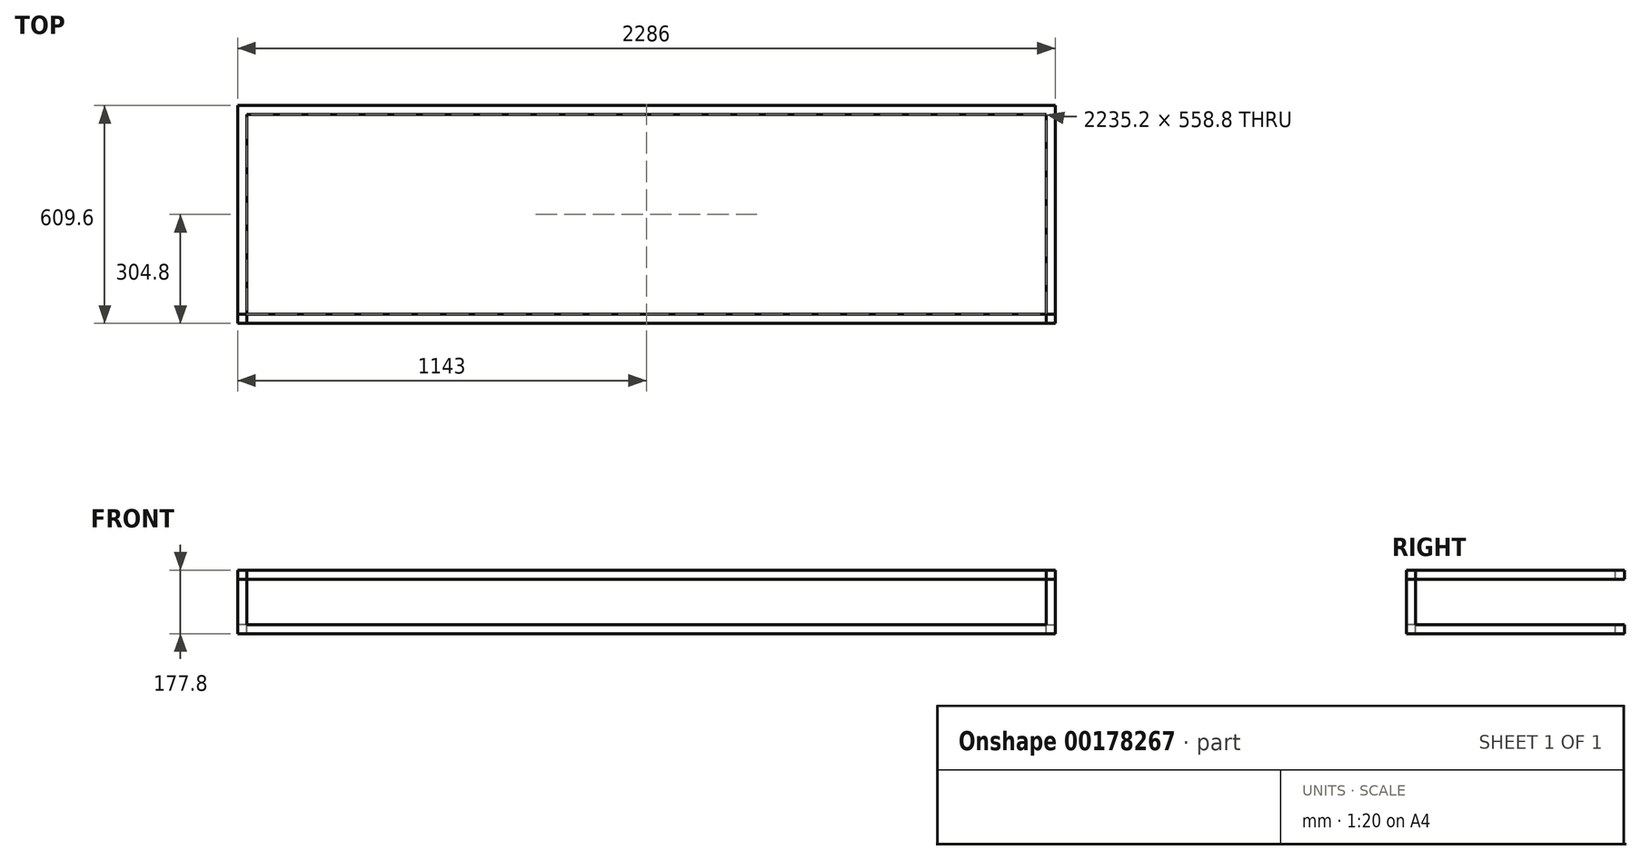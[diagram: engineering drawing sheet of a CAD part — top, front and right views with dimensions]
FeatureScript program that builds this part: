
annotation { "Feature Type Name" : "Feature", "Feature Type Description" : "" }
export const myFeature = defineFeature(function(context is Context, id is Id, definition is map)
    precondition{}
    {
        {
            var Q0;
            Q0=qCreatedBy(makeId("Top.planeOp"),FACE);
            var sketch = newSketch(context, id + "F0", { "sketchPlane" : qUnion([Q0])});
            skLineSegment(sketch, "E0.bottom", {"start": v(-1143, -304.8) * mm, "end": v(1143, -304.8) * mm});
            skLineSegment(sketch, "E0.top", {"start": v(-1143, 304.8) * mm, "end": v(1143, 304.8) * mm});
            skLineSegment(sketch, "E0.left", {"start": v(-1143, -304.8) * mm, "end": v(-1143, 304.8) * mm});
            skLineSegment(sketch, "E0.right", {"start": v(1143, -304.8) * mm, "end": v(1143, 304.8) * mm});
            skPoint(sketch, "E0.middle", {"position": v(0, 0) * mm});
            skLineSegment(sketch, "E1.bottom", {"start": v(-1117.6, -279.4) * mm, "end": v(1117.6, -279.4) * mm});
            skLineSegment(sketch, "E1.top", {"start": v(-1117.6, 279.4) * mm, "end": v(1117.6, 279.4) * mm});
            skLineSegment(sketch, "E1.left", {"start": v(-1117.6, -279.4) * mm, "end": v(-1117.6, 279.4) * mm});
            skLineSegment(sketch, "E1.right", {"start": v(1117.6, -279.4) * mm, "end": v(1117.6, 279.4) * mm});
            skLineSegment(sketch, "E2", {"start": v(-1143, 304.8) * mm, "end": v(-1117.6, 304.8) * mm});
            skLineSegment(sketch, "E3", {"start": v(-1117.6, 304.8) * mm, "end": v(-1117.6, 279.4) * mm});
            skLineSegment(sketch, "E4", {"start": v(-1143, 279.4) * mm, "end": v(-1143, 304.8) * mm});
            skLineSegment(sketch, "E5.bottom", {"start": v(1143, 304.8) * mm, "end": v(1117.6, 304.8) * mm});
            skLineSegment(sketch, "E5.top", {"start": v(1143, 279.4) * mm, "end": v(1117.6, 279.4) * mm});
            skLineSegment(sketch, "E5.left", {"start": v(1143, 304.8) * mm, "end": v(1143, 279.4) * mm});
            skLineSegment(sketch, "E5.right", {"start": v(1117.6, 304.8) * mm, "end": v(1117.6, 279.4) * mm});
            skLineSegment(sketch, "E6.bottom", {"start": v(1117.6, -279.4) * mm, "end": v(1143, -279.4) * mm});
            skLineSegment(sketch, "E6.top", {"start": v(1117.6, -304.8) * mm, "end": v(1143, -304.8) * mm});
            skLineSegment(sketch, "E6.left", {"start": v(1117.6, -279.4) * mm, "end": v(1117.6, -304.8) * mm});
            skLineSegment(sketch, "E6.right", {"start": v(1143, -279.4) * mm, "end": v(1143, -304.8) * mm});
            skLineSegment(sketch, "E7.bottom", {"start": v(-1117.6, -279.4) * mm, "end": v(-1143, -279.4) * mm});
            skLineSegment(sketch, "E7.top", {"start": v(-1117.6, -304.8) * mm, "end": v(-1143, -304.8) * mm});
            skLineSegment(sketch, "E7.left", {"start": v(-1117.6, -279.4) * mm, "end": v(-1117.6, -304.8) * mm});
            skLineSegment(sketch, "E7.right", {"start": v(-1143, -279.4) * mm, "end": v(-1143, -304.8) * mm});
            skLineSegment(sketch, "E8", {"start": v(-1143, 279.4) * mm, "end": v(-1117.6, 279.4) * mm});
            skSolve(sketch);
        }
        {
            var Q0;
            Q0 = qSketchRegion(id + "F0", true);
            extrude(context, id + "F1", {"entities" : qUnion([Q0]), "oppositeDirection" : true, "depth" : 25.4 * mm});
        }
        {
            var Q0;
            Q0=makeQuery(id+"F0.imprint","IMPRINT",FACE,{"disambiguationData":[TD([[makeQuery(id+"F0.imprint","IMPRINT",EDGE,{"derivedFrom":sQuery(id+"F0.wireOp",EDGE,"E2")}),-1.0]])]});
            var Q1;
            Q1=makeQuery(id+"F0.imprint","IMPRINT",FACE,{"disambiguationData":[TD([[makeQuery(id+"F0.imprint","IMPRINT",EDGE,{"derivedFrom":sQuery(id+"F0.wireOp",EDGE,"E7.bottom")}),1.0]])]});
            var Q2;
            Q2=makeQuery(id+"F0.imprint","IMPRINT",FACE,{"disambiguationData":[TD([[makeQuery(id+"F0.imprint","IMPRINT",EDGE,{"derivedFrom":sQuery(id+"F0.wireOp",EDGE,"E5.bottom")}),1.0]])]});
            var Q3;
            Q3=makeQuery(id+"F0.imprint","IMPRINT",FACE,{"disambiguationData":[TD([[makeQuery(id+"F0.imprint","IMPRINT",EDGE,{"derivedFrom":sQuery(id+"F0.wireOp",EDGE,"E6.bottom")}),-1.0]])]});
            extrude(context, id + "F2", {"entities" : qUnion([Q0, Q1, Q2, Q3]), "operationType" : NewBodyOperationType.ADD, "depth" : 152.4 * mm});
        }
        {
            var Q0;
            Q0=qCreatedBy(makeId("Top.planeOp"),FACE);
            cPlane(context, id + "F3", {"entities" : qUnion([Q0]), "cplaneType" : CPlaneType.OFFSET, "offset" : 152.4 * mm, "width" : 152.4 * mm, "height" : 152.4 * mm});
        }
        {
            var Q0;
            Q0=qCreatedBy(id+"F3.planeOp",FACE);
            var sketch = newSketch(context, id + "F4", { "sketchPlane" : qUnion([Q0])});
            skLineSegment(sketch, "E9.0", {"start": v(-1117.6, 279.4) * mm, "end": v(1117.6, 279.4) * mm});
            skLineSegment(sketch, "E10.0", {"start": v(-1143, 304.8) * mm, "end": v(1143, 304.8) * mm});
            skLineSegment(sketch, "E11.0", {"start": v(-1117.6, -279.4) * mm, "end": v(-1117.6, 279.4) * mm});
            skLineSegment(sketch, "E12.0", {"start": v(-1143, -304.8) * mm, "end": v(-1143, 304.8) * mm});
            skLineSegment(sketch, "E13.0", {"start": v(-1117.6, -279.4) * mm, "end": v(1117.6, -279.4) * mm});
            skLineSegment(sketch, "E14.0", {"start": v(-1143, -304.8) * mm, "end": v(1143, -304.8) * mm});
            skLineSegment(sketch, "E15.0", {"start": v(1117.6, -279.4) * mm, "end": v(1117.6, 279.4) * mm});
            skLineSegment(sketch, "E16.0", {"start": v(1143, 304.8) * mm, "end": v(1143, -304.8) * mm});
            skSolve(sketch);
        }
        {
            var Q0;
            Q0=makeQuery(id+"F4.imprint","IMPRINT",FACE,{"disambiguationData":[TD([[makeQuery(id+"F4.imprint","IMPRINT",EDGE,{"derivedFrom":sQuery(id+"F4.wireOp",EDGE,"E9.0")}),1.0]])]});
            extrude(context, id + "F5", {"entities" : qUnion([Q0]), "oppositeDirection" : true, "depth" : 25.4 * mm});
        }
    });
